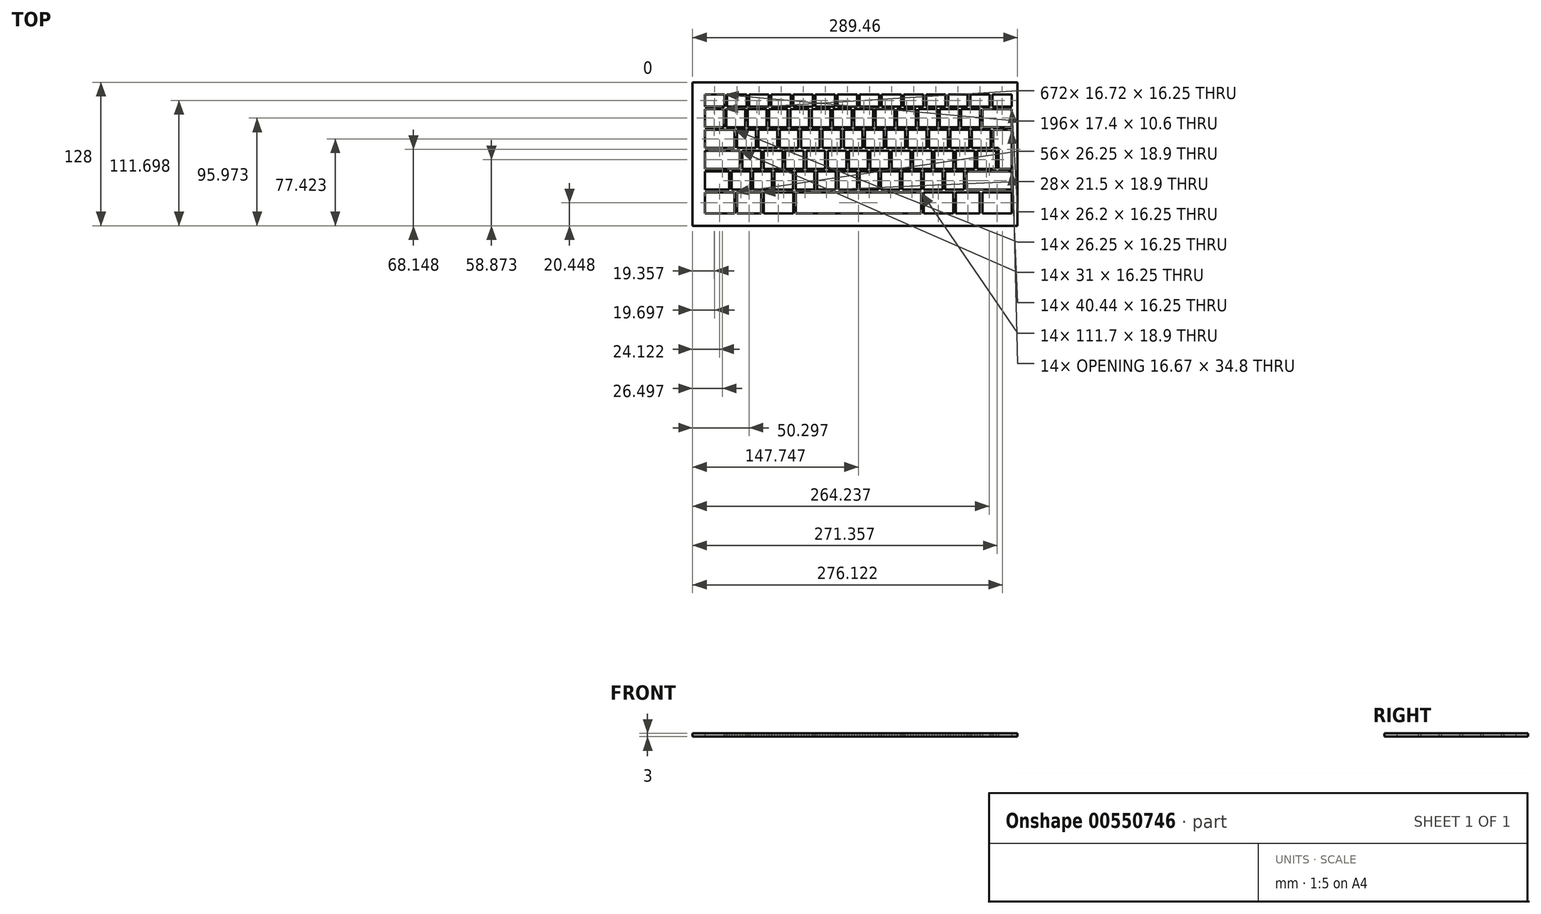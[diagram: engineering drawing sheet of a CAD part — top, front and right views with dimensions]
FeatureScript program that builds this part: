
annotation { "Feature Type Name" : "Feature", "Feature Type Description" : "" }
export const myFeature = defineFeature(function(context is Context, id is Id, definition is map)
    precondition{}
    {
        {
            var Q0;
            Q0=qCreatedBy(makeId("Top.planeOp"),FACE);
            var sketch = newSketch(context, id + "F0", { "sketchPlane" : qUnion([Q0])});
            skLineSegment(sketch, "E0.bottom", {"start": v(-207.41, -87.25) * mm, "end": v(222.59, -87.25) * mm, "construction": true});
            skLineSegment(sketch, "E0.top", {"start": v(-207.41, -201.25) * mm, "end": v(222.59, -201.25) * mm, "construction": true});
            skLineSegment(sketch, "E0.left", {"start": v(-207.41, -87.25) * mm, "end": v(-207.41, -201.25) * mm, "construction": true});
            skLineSegment(sketch, "E1.bottom", {"start": v(-203.41, -91.25) * mm, "end": v(-186.01, -91.25) * mm});
            skLineSegment(sketch, "E1.top", {"start": v(-203.41, -101.85) * mm, "end": v(-186.01, -101.85) * mm});
            skLineSegment(sketch, "E1.left", {"start": v(-203.41, -91.25) * mm, "end": v(-203.41, -101.85) * mm});
            skLineSegment(sketch, "E1.right", {"start": v(-186.01, -91.25) * mm, "end": v(-186.01, -101.85) * mm});
            skPoint(sketch, "E1.middle", {"position": v(-194.71, -96.55) * mm});
            skLineSegment(sketch, "E2.1.0.0", {"start": v(-166.31, -91.25) * mm, "end": v(-166.31, -101.85) * mm});
            skPoint(sketch, "E2.1.0.1", {"position": v(-175.01, -96.55) * mm});
            skLineSegment(sketch, "E2.1.0.2", {"start": v(-183.71, -91.25) * mm, "end": v(-183.71, -101.85) * mm});
            skLineSegment(sketch, "E2.1.0.3", {"start": v(-183.71, -101.85) * mm, "end": v(-166.31, -101.85) * mm});
            skLineSegment(sketch, "E2.1.0.4", {"start": v(-183.71, -91.25) * mm, "end": v(-166.31, -91.25) * mm});
            skLineSegment(sketch, "E2.2.0.0", {"start": v(-146.61, -91.25) * mm, "end": v(-146.61, -101.85) * mm});
            skPoint(sketch, "E2.2.0.1", {"position": v(-155.31, -96.55) * mm});
            skLineSegment(sketch, "E2.2.0.2", {"start": v(-164.01, -91.25) * mm, "end": v(-164.01, -101.85) * mm});
            skLineSegment(sketch, "E2.2.0.3", {"start": v(-164.01, -101.85) * mm, "end": v(-146.61, -101.85) * mm});
            skLineSegment(sketch, "E2.2.0.4", {"start": v(-164.01, -91.25) * mm, "end": v(-146.61, -91.25) * mm});
            skLineSegment(sketch, "E2.3.0.0", {"start": v(-126.91, -91.25) * mm, "end": v(-126.91, -101.85) * mm});
            skPoint(sketch, "E2.3.0.1", {"position": v(-135.61, -96.55) * mm});
            skLineSegment(sketch, "E2.3.0.2", {"start": v(-144.31, -91.25) * mm, "end": v(-144.31, -101.85) * mm});
            skLineSegment(sketch, "E2.3.0.3", {"start": v(-144.31, -101.85) * mm, "end": v(-126.91, -101.85) * mm});
            skLineSegment(sketch, "E2.3.0.4", {"start": v(-144.31, -91.25) * mm, "end": v(-126.91, -91.25) * mm});
            skLineSegment(sketch, "E2.4.0.0", {"start": v(-107.21, -91.25) * mm, "end": v(-107.21, -101.85) * mm});
            skPoint(sketch, "E2.4.0.1", {"position": v(-115.91, -96.55) * mm});
            skLineSegment(sketch, "E2.4.0.2", {"start": v(-124.61, -91.25) * mm, "end": v(-124.61, -101.85) * mm});
            skLineSegment(sketch, "E2.4.0.3", {"start": v(-124.61, -101.85) * mm, "end": v(-107.21, -101.85) * mm});
            skLineSegment(sketch, "E2.4.0.4", {"start": v(-124.61, -91.25) * mm, "end": v(-107.21, -91.25) * mm});
            skLineSegment(sketch, "E2.5.0.0", {"start": v(-87.51, -91.25) * mm, "end": v(-87.51, -101.85) * mm});
            skPoint(sketch, "E2.5.0.1", {"position": v(-96.21, -96.55) * mm});
            skLineSegment(sketch, "E2.5.0.2", {"start": v(-104.91, -91.25) * mm, "end": v(-104.91, -101.85) * mm});
            skLineSegment(sketch, "E2.5.0.3", {"start": v(-104.91, -101.85) * mm, "end": v(-87.51, -101.85) * mm});
            skLineSegment(sketch, "E2.5.0.4", {"start": v(-104.91, -91.25) * mm, "end": v(-87.51, -91.25) * mm});
            skLineSegment(sketch, "E2.6.0.0", {"start": v(-67.81, -91.25) * mm, "end": v(-67.81, -101.85) * mm});
            skPoint(sketch, "E2.6.0.1", {"position": v(-76.51, -96.55) * mm});
            skLineSegment(sketch, "E2.6.0.2", {"start": v(-85.21, -91.25) * mm, "end": v(-85.21, -101.85) * mm});
            skLineSegment(sketch, "E2.6.0.3", {"start": v(-85.21, -101.85) * mm, "end": v(-67.81, -101.85) * mm});
            skLineSegment(sketch, "E2.6.0.4", {"start": v(-85.21, -91.25) * mm, "end": v(-67.81, -91.25) * mm});
            skLineSegment(sketch, "E2.7.0.0", {"start": v(-48.11, -91.25) * mm, "end": v(-48.11, -101.85) * mm});
            skPoint(sketch, "E2.7.0.1", {"position": v(-56.81, -96.55) * mm});
            skLineSegment(sketch, "E2.7.0.2", {"start": v(-65.51, -91.25) * mm, "end": v(-65.51, -101.85) * mm});
            skLineSegment(sketch, "E2.7.0.3", {"start": v(-65.51, -101.85) * mm, "end": v(-48.11, -101.85) * mm});
            skLineSegment(sketch, "E2.7.0.4", {"start": v(-65.51, -91.25) * mm, "end": v(-48.11, -91.25) * mm});
            skLineSegment(sketch, "E2.8.0.0", {"start": v(-28.41, -91.25) * mm, "end": v(-28.41, -101.85) * mm});
            skPoint(sketch, "E2.8.0.1", {"position": v(-37.11, -96.55) * mm});
            skLineSegment(sketch, "E2.8.0.2", {"start": v(-45.81, -91.25) * mm, "end": v(-45.81, -101.85) * mm});
            skLineSegment(sketch, "E2.8.0.3", {"start": v(-45.81, -101.85) * mm, "end": v(-28.41, -101.85) * mm});
            skLineSegment(sketch, "E2.8.0.4", {"start": v(-45.81, -91.25) * mm, "end": v(-28.41, -91.25) * mm});
            skLineSegment(sketch, "E2.9.0.0", {"start": v(-8.71, -91.25) * mm, "end": v(-8.71, -101.85) * mm});
            skPoint(sketch, "E2.9.0.1", {"position": v(-17.41, -96.55) * mm});
            skLineSegment(sketch, "E2.9.0.2", {"start": v(-26.11, -91.25) * mm, "end": v(-26.11, -101.85) * mm});
            skLineSegment(sketch, "E2.9.0.3", {"start": v(-26.11, -101.85) * mm, "end": v(-8.71, -101.85) * mm});
            skLineSegment(sketch, "E2.9.0.4", {"start": v(-26.11, -91.25) * mm, "end": v(-8.71, -91.25) * mm});
            skLineSegment(sketch, "E2.10.0.0", {"start": v(10.99, -91.25) * mm, "end": v(10.99, -101.85) * mm});
            skPoint(sketch, "E2.10.0.1", {"position": v(2.29, -96.55) * mm});
            skLineSegment(sketch, "E2.10.0.2", {"start": v(-6.41, -91.25) * mm, "end": v(-6.41, -101.85) * mm});
            skLineSegment(sketch, "E2.10.0.3", {"start": v(-6.41, -101.85) * mm, "end": v(10.99, -101.85) * mm});
            skLineSegment(sketch, "E2.10.0.4", {"start": v(-6.41, -91.25) * mm, "end": v(10.99, -91.25) * mm});
            skLineSegment(sketch, "E2.11.0.0", {"start": v(30.69, -91.25) * mm, "end": v(30.69, -101.85) * mm});
            skPoint(sketch, "E2.11.0.1", {"position": v(21.99, -96.55) * mm});
            skLineSegment(sketch, "E2.11.0.2", {"start": v(13.29, -91.25) * mm, "end": v(13.29, -101.85) * mm});
            skLineSegment(sketch, "E2.11.0.3", {"start": v(13.29, -101.85) * mm, "end": v(30.69, -101.85) * mm});
            skLineSegment(sketch, "E2.11.0.4", {"start": v(13.29, -91.25) * mm, "end": v(30.69, -91.25) * mm});
            skLineSegment(sketch, "E2.12.0.0", {"start": v(50.39, -91.25) * mm, "end": v(50.39, -101.85) * mm});
            skPoint(sketch, "E2.12.0.1", {"position": v(41.69, -96.55) * mm});
            skLineSegment(sketch, "E2.12.0.2", {"start": v(32.99, -91.25) * mm, "end": v(32.99, -101.85) * mm});
            skLineSegment(sketch, "E2.12.0.3", {"start": v(32.99, -101.85) * mm, "end": v(50.39, -101.85) * mm});
            skLineSegment(sketch, "E2.12.0.4", {"start": v(32.99, -91.25) * mm, "end": v(50.39, -91.25) * mm});
            skLineSegment(sketch, "E2.13.0.0", {"start": v(70.09, -91.25) * mm, "end": v(70.09, -101.85) * mm});
            skPoint(sketch, "E2.13.0.1", {"position": v(61.39, -96.55) * mm});
            skLineSegment(sketch, "E2.13.0.2", {"start": v(52.69, -91.25) * mm, "end": v(52.69, -101.85) * mm});
            skLineSegment(sketch, "E2.13.0.3", {"start": v(52.69, -101.85) * mm, "end": v(70.09, -101.85) * mm});
            skLineSegment(sketch, "E2.13.0.4", {"start": v(52.69, -91.25) * mm, "end": v(70.09, -91.25) * mm});
            skLineSegment(sketch, "E3.bottom", {"start": v(-203.41, -104.15) * mm, "end": v(-186.7, -104.15) * mm});
            skLineSegment(sketch, "E3.top", {"start": v(-203.41, -120.4) * mm, "end": v(-186.7, -120.4) * mm});
            skLineSegment(sketch, "E3.left", {"start": v(-203.41, -104.15) * mm, "end": v(-203.41, -120.4) * mm});
            skLineSegment(sketch, "E3.right", {"start": v(-186.7, -104.15) * mm, "end": v(-186.7, -120.4) * mm});
            skPoint(sketch, "E3.middle", {"position": v(-195.05, -112.28) * mm});
            skPoint(sketch, "E4.1.0.0", {"position": v(-176.03, -112.28) * mm});
            skLineSegment(sketch, "E4.1.0.1", {"start": v(-167.67, -104.15) * mm, "end": v(-167.67, -120.4) * mm});
            skLineSegment(sketch, "E4.1.0.2", {"start": v(-184.4, -104.15) * mm, "end": v(-167.67, -104.15) * mm});
            skLineSegment(sketch, "E4.1.0.3", {"start": v(-184.4, -104.15) * mm, "end": v(-184.4, -120.4) * mm});
            skLineSegment(sketch, "E4.1.0.4", {"start": v(-184.4, -120.4) * mm, "end": v(-167.67, -120.4) * mm});
            skPoint(sketch, "E4.2.0.0", {"position": v(-157.01, -112.28) * mm});
            skLineSegment(sketch, "E4.2.0.1", {"start": v(-148.65, -104.15) * mm, "end": v(-148.65, -120.4) * mm});
            skLineSegment(sketch, "E4.2.0.2", {"start": v(-165.37, -104.15) * mm, "end": v(-148.65, -104.15) * mm});
            skLineSegment(sketch, "E4.2.0.3", {"start": v(-165.37, -104.15) * mm, "end": v(-165.37, -120.4) * mm});
            skLineSegment(sketch, "E4.2.0.4", {"start": v(-165.37, -120.4) * mm, "end": v(-148.65, -120.4) * mm});
            skPoint(sketch, "E4.3.0.0", {"position": v(-138, -112.28) * mm});
            skLineSegment(sketch, "E4.3.0.1", {"start": v(-129.63, -104.15) * mm, "end": v(-129.63, -120.4) * mm});
            skLineSegment(sketch, "E4.3.0.2", {"start": v(-146.35, -104.15) * mm, "end": v(-129.63, -104.15) * mm});
            skLineSegment(sketch, "E4.3.0.3", {"start": v(-146.35, -104.15) * mm, "end": v(-146.35, -120.4) * mm});
            skLineSegment(sketch, "E4.3.0.4", {"start": v(-146.35, -120.4) * mm, "end": v(-129.63, -120.4) * mm});
            skPoint(sketch, "E4.4.0.0", {"position": v(-118.97, -112.28) * mm});
            skLineSegment(sketch, "E4.4.0.1", {"start": v(-110.61, -104.15) * mm, "end": v(-110.61, -120.4) * mm});
            skLineSegment(sketch, "E4.4.0.2", {"start": v(-127.33, -104.15) * mm, "end": v(-110.61, -104.15) * mm});
            skLineSegment(sketch, "E4.4.0.3", {"start": v(-127.33, -104.15) * mm, "end": v(-127.33, -120.4) * mm});
            skLineSegment(sketch, "E4.4.0.4", {"start": v(-127.33, -120.4) * mm, "end": v(-110.61, -120.4) * mm});
            skPoint(sketch, "E4.5.0.0", {"position": v(-99.95, -112.28) * mm});
            skLineSegment(sketch, "E4.5.0.1", {"start": v(-91.6, -104.15) * mm, "end": v(-91.6, -120.4) * mm});
            skLineSegment(sketch, "E4.5.0.2", {"start": v(-108.31, -104.15) * mm, "end": v(-91.6, -104.15) * mm});
            skLineSegment(sketch, "E4.5.0.3", {"start": v(-108.31, -104.15) * mm, "end": v(-108.31, -120.4) * mm});
            skLineSegment(sketch, "E4.5.0.4", {"start": v(-108.31, -120.4) * mm, "end": v(-91.6, -120.4) * mm});
            skPoint(sketch, "E4.6.0.0", {"position": v(-80.93, -112.28) * mm});
            skLineSegment(sketch, "E4.6.0.1", {"start": v(-72.57, -104.15) * mm, "end": v(-72.57, -120.4) * mm});
            skLineSegment(sketch, "E4.6.0.2", {"start": v(-89.3, -104.15) * mm, "end": v(-72.57, -104.15) * mm});
            skLineSegment(sketch, "E4.6.0.3", {"start": v(-89.3, -104.15) * mm, "end": v(-89.3, -120.4) * mm});
            skLineSegment(sketch, "E4.6.0.4", {"start": v(-89.3, -120.4) * mm, "end": v(-72.57, -120.4) * mm});
            skPoint(sketch, "E4.7.0.0", {"position": v(-61.91, -112.28) * mm});
            skLineSegment(sketch, "E4.7.0.1", {"start": v(-53.55, -104.15) * mm, "end": v(-53.55, -120.4) * mm});
            skLineSegment(sketch, "E4.7.0.2", {"start": v(-70.27, -104.15) * mm, "end": v(-53.55, -104.15) * mm});
            skLineSegment(sketch, "E4.7.0.3", {"start": v(-70.27, -104.15) * mm, "end": v(-70.27, -120.4) * mm});
            skLineSegment(sketch, "E4.7.0.4", {"start": v(-70.27, -120.4) * mm, "end": v(-53.55, -120.4) * mm});
            skPoint(sketch, "E4.8.0.0", {"position": v(-42.9, -112.28) * mm});
            skLineSegment(sketch, "E4.8.0.1", {"start": v(-34.53, -104.15) * mm, "end": v(-34.53, -120.4) * mm});
            skLineSegment(sketch, "E4.8.0.2", {"start": v(-51.25, -104.15) * mm, "end": v(-34.53, -104.15) * mm});
            skLineSegment(sketch, "E4.8.0.3", {"start": v(-51.25, -104.15) * mm, "end": v(-51.25, -120.4) * mm});
            skLineSegment(sketch, "E4.8.0.4", {"start": v(-51.25, -120.4) * mm, "end": v(-34.53, -120.4) * mm});
            skPoint(sketch, "E4.9.0.0", {"position": v(-23.87, -112.28) * mm});
            skLineSegment(sketch, "E4.9.0.1", {"start": v(-15.51, -104.15) * mm, "end": v(-15.51, -120.4) * mm});
            skLineSegment(sketch, "E4.9.0.2", {"start": v(-32.23, -104.15) * mm, "end": v(-15.51, -104.15) * mm});
            skLineSegment(sketch, "E4.9.0.3", {"start": v(-32.23, -104.15) * mm, "end": v(-32.23, -120.4) * mm});
            skLineSegment(sketch, "E4.9.0.4", {"start": v(-32.23, -120.4) * mm, "end": v(-15.51, -120.4) * mm});
            skPoint(sketch, "E4.10.0.0", {"position": v(-4.85, -112.28) * mm});
            skLineSegment(sketch, "E4.10.0.1", {"start": v(3.5, -104.15) * mm, "end": v(3.5, -120.4) * mm});
            skLineSegment(sketch, "E4.10.0.2", {"start": v(-13.21, -104.15) * mm, "end": v(3.5, -104.15) * mm});
            skLineSegment(sketch, "E4.10.0.3", {"start": v(-13.21, -104.15) * mm, "end": v(-13.21, -120.4) * mm});
            skLineSegment(sketch, "E4.10.0.4", {"start": v(-13.21, -120.4) * mm, "end": v(3.5, -120.4) * mm});
            skPoint(sketch, "E4.11.0.0", {"position": v(14.17, -112.28) * mm});
            skLineSegment(sketch, "E4.11.0.1", {"start": v(22.53, -104.15) * mm, "end": v(22.53, -120.4) * mm});
            skLineSegment(sketch, "E4.11.0.2", {"start": v(5.8, -104.15) * mm, "end": v(22.53, -104.15) * mm});
            skLineSegment(sketch, "E4.11.0.3", {"start": v(5.8, -104.15) * mm, "end": v(5.8, -120.4) * mm});
            skLineSegment(sketch, "E4.11.0.4", {"start": v(5.8, -120.4) * mm, "end": v(22.53, -120.4) * mm});
            skPoint(sketch, "E4.12.0.0", {"position": v(33.19, -112.28) * mm});
            skLineSegment(sketch, "E4.12.0.1", {"start": v(41.55, -104.15) * mm, "end": v(41.55, -120.4) * mm});
            skLineSegment(sketch, "E4.12.0.2", {"start": v(24.83, -104.15) * mm, "end": v(41.55, -104.15) * mm});
            skLineSegment(sketch, "E4.12.0.3", {"start": v(24.83, -104.15) * mm, "end": v(24.83, -120.4) * mm});
            skLineSegment(sketch, "E4.12.0.4", {"start": v(24.83, -120.4) * mm, "end": v(41.55, -120.4) * mm});
            skLineSegment(sketch, "E5.bottom", {"start": v(43.85, -104.15) * mm, "end": v(70.05, -104.15) * mm});
            skLineSegment(sketch, "E5.top", {"start": v(43.85, -120.4) * mm, "end": v(70.05, -120.4) * mm});
            skLineSegment(sketch, "E5.left", {"start": v(43.85, -104.15) * mm, "end": v(43.85, -120.4) * mm});
            skLineSegment(sketch, "E5.right", {"start": v(70.05, -104.15) * mm, "end": v(70.05, -120.4) * mm});
            skPoint(sketch, "E5.middle", {"position": v(56.95, -112.28) * mm});
            skLineSegment(sketch, "E6.bottom", {"start": v(-203.41, -122.7) * mm, "end": v(-177.16, -122.7) * mm});
            skLineSegment(sketch, "E6.top", {"start": v(-203.41, -138.95) * mm, "end": v(-177.16, -138.95) * mm});
            skLineSegment(sketch, "E6.left", {"start": v(-203.41, -122.7) * mm, "end": v(-203.41, -138.95) * mm});
            skLineSegment(sketch, "E6.right", {"start": v(-177.16, -122.7) * mm, "end": v(-177.16, -138.95) * mm});
            skPoint(sketch, "E6.middle", {"position": v(-190.29, -130.83) * mm});
            skLineSegment(sketch, "E7.bottom", {"start": v(-174.86, -122.7) * mm, "end": v(-158.14, -122.7) * mm});
            skLineSegment(sketch, "E7.top", {"start": v(-174.86, -138.95) * mm, "end": v(-158.14, -138.95) * mm});
            skLineSegment(sketch, "E7.left", {"start": v(-174.86, -122.7) * mm, "end": v(-174.86, -138.95) * mm});
            skLineSegment(sketch, "E7.right", {"start": v(-158.14, -122.7) * mm, "end": v(-158.14, -138.95) * mm});
            skPoint(sketch, "E7.middle", {"position": v(-166.5, -130.83) * mm});
            skLineSegment(sketch, "E8.1.0.0", {"start": v(-139.12, -122.7) * mm, "end": v(-139.12, -138.95) * mm});
            skLineSegment(sketch, "E8.1.0.1", {"start": v(-155.84, -122.7) * mm, "end": v(-155.84, -138.95) * mm});
            skLineSegment(sketch, "E8.1.0.2", {"start": v(-155.84, -122.7) * mm, "end": v(-139.12, -122.7) * mm});
            skPoint(sketch, "E8.1.0.3", {"position": v(-147.48, -130.83) * mm});
            skLineSegment(sketch, "E8.1.0.4", {"start": v(-155.84, -138.95) * mm, "end": v(-139.12, -138.95) * mm});
            skLineSegment(sketch, "E8.2.0.0", {"start": v(-120.1, -122.7) * mm, "end": v(-120.1, -138.95) * mm});
            skLineSegment(sketch, "E8.2.0.1", {"start": v(-136.82, -122.7) * mm, "end": v(-136.82, -138.95) * mm});
            skLineSegment(sketch, "E8.2.0.2", {"start": v(-136.82, -122.7) * mm, "end": v(-120.1, -122.7) * mm});
            skPoint(sketch, "E8.2.0.3", {"position": v(-128.46, -130.83) * mm});
            skLineSegment(sketch, "E8.2.0.4", {"start": v(-136.82, -138.95) * mm, "end": v(-120.1, -138.95) * mm});
            skLineSegment(sketch, "E8.3.0.0", {"start": v(-101.08, -122.7) * mm, "end": v(-101.08, -138.95) * mm});
            skLineSegment(sketch, "E8.3.0.1", {"start": v(-117.8, -122.7) * mm, "end": v(-117.8, -138.95) * mm});
            skLineSegment(sketch, "E8.3.0.2", {"start": v(-117.8, -122.7) * mm, "end": v(-101.08, -122.7) * mm});
            skPoint(sketch, "E8.3.0.3", {"position": v(-109.44, -130.83) * mm});
            skLineSegment(sketch, "E8.3.0.4", {"start": v(-117.8, -138.95) * mm, "end": v(-101.08, -138.95) * mm});
            skLineSegment(sketch, "E8.4.0.0", {"start": v(-82.06, -122.7) * mm, "end": v(-82.06, -138.95) * mm});
            skLineSegment(sketch, "E8.4.0.1", {"start": v(-98.78, -122.7) * mm, "end": v(-98.78, -138.95) * mm});
            skLineSegment(sketch, "E8.4.0.2", {"start": v(-98.78, -122.7) * mm, "end": v(-82.06, -122.7) * mm});
            skPoint(sketch, "E8.4.0.3", {"position": v(-90.42, -130.83) * mm});
            skLineSegment(sketch, "E8.4.0.4", {"start": v(-98.78, -138.95) * mm, "end": v(-82.06, -138.95) * mm});
            skLineSegment(sketch, "E8.5.0.0", {"start": v(-63.04, -122.7) * mm, "end": v(-63.04, -138.95) * mm});
            skLineSegment(sketch, "E8.5.0.1", {"start": v(-79.76, -122.7) * mm, "end": v(-79.76, -138.95) * mm});
            skLineSegment(sketch, "E8.5.0.2", {"start": v(-79.76, -122.7) * mm, "end": v(-63.04, -122.7) * mm});
            skPoint(sketch, "E8.5.0.3", {"position": v(-71.4, -130.83) * mm});
            skLineSegment(sketch, "E8.5.0.4", {"start": v(-79.76, -138.95) * mm, "end": v(-63.04, -138.95) * mm});
            skLineSegment(sketch, "E8.6.0.0", {"start": v(-44.02, -122.7) * mm, "end": v(-44.02, -138.95) * mm});
            skLineSegment(sketch, "E8.6.0.1", {"start": v(-60.74, -122.7) * mm, "end": v(-60.74, -138.95) * mm});
            skLineSegment(sketch, "E8.6.0.2", {"start": v(-60.74, -122.7) * mm, "end": v(-44.02, -122.7) * mm});
            skPoint(sketch, "E8.6.0.3", {"position": v(-52.38, -130.83) * mm});
            skLineSegment(sketch, "E8.6.0.4", {"start": v(-60.74, -138.95) * mm, "end": v(-44.02, -138.95) * mm});
            skLineSegment(sketch, "E8.7.0.0", {"start": v(-25, -122.7) * mm, "end": v(-25, -138.95) * mm});
            skLineSegment(sketch, "E8.7.0.1", {"start": v(-41.72, -122.7) * mm, "end": v(-41.72, -138.95) * mm});
            skLineSegment(sketch, "E8.7.0.2", {"start": v(-41.72, -122.7) * mm, "end": v(-25, -122.7) * mm});
            skPoint(sketch, "E8.7.0.3", {"position": v(-33.36, -130.83) * mm});
            skLineSegment(sketch, "E8.7.0.4", {"start": v(-41.72, -138.95) * mm, "end": v(-25, -138.95) * mm});
            skLineSegment(sketch, "E8.8.0.0", {"start": v(-5.98, -122.7) * mm, "end": v(-5.98, -138.95) * mm});
            skLineSegment(sketch, "E8.8.0.1", {"start": v(-22.7, -122.7) * mm, "end": v(-22.7, -138.95) * mm});
            skLineSegment(sketch, "E8.8.0.2", {"start": v(-22.7, -122.7) * mm, "end": v(-5.98, -122.7) * mm});
            skPoint(sketch, "E8.8.0.3", {"position": v(-14.34, -130.83) * mm});
            skLineSegment(sketch, "E8.8.0.4", {"start": v(-22.7, -138.95) * mm, "end": v(-5.98, -138.95) * mm});
            skLineSegment(sketch, "E8.9.0.0", {"start": v(13.04, -122.7) * mm, "end": v(13.04, -138.95) * mm});
            skLineSegment(sketch, "E8.9.0.1", {"start": v(-3.68, -122.7) * mm, "end": v(-3.68, -138.95) * mm});
            skLineSegment(sketch, "E8.9.0.2", {"start": v(-3.68, -122.7) * mm, "end": v(13.04, -122.7) * mm});
            skPoint(sketch, "E8.9.0.3", {"position": v(4.68, -130.83) * mm});
            skLineSegment(sketch, "E8.9.0.4", {"start": v(-3.68, -138.95) * mm, "end": v(13.04, -138.95) * mm});
            skLineSegment(sketch, "E8.10.0.0", {"start": v(32.06, -122.7) * mm, "end": v(32.06, -138.95) * mm});
            skLineSegment(sketch, "E8.10.0.1", {"start": v(15.34, -122.7) * mm, "end": v(15.34, -138.95) * mm});
            skLineSegment(sketch, "E8.10.0.2", {"start": v(15.34, -122.7) * mm, "end": v(32.06, -122.7) * mm});
            skPoint(sketch, "E8.10.0.3", {"position": v(23.7, -130.83) * mm});
            skLineSegment(sketch, "E8.10.0.4", {"start": v(15.34, -138.95) * mm, "end": v(32.06, -138.95) * mm});
            skLineSegment(sketch, "E8.11.0.0", {"start": v(51.08, -122.7) * mm, "end": v(51.08, -138.95) * mm});
            skLineSegment(sketch, "E8.11.0.1", {"start": v(34.36, -122.7) * mm, "end": v(34.36, -138.95) * mm});
            skLineSegment(sketch, "E8.11.0.2", {"start": v(34.36, -122.7) * mm, "end": v(51.08, -122.7) * mm});
            skPoint(sketch, "E8.11.0.3", {"position": v(42.72, -130.83) * mm});
            skLineSegment(sketch, "E8.11.0.4", {"start": v(34.36, -138.95) * mm, "end": v(51.08, -138.95) * mm});
            skLineSegment(sketch, "E9.bottom", {"start": v(-203.41, -141.25) * mm, "end": v(-172.41, -141.25) * mm});
            skLineSegment(sketch, "E9.top", {"start": v(-203.41, -157.5) * mm, "end": v(-172.41, -157.5) * mm});
            skLineSegment(sketch, "E9.left", {"start": v(-203.41, -141.25) * mm, "end": v(-203.41, -157.5) * mm});
            skLineSegment(sketch, "E9.right", {"start": v(-172.41, -141.25) * mm, "end": v(-172.41, -157.5) * mm});
            skPoint(sketch, "E9.middle", {"position": v(-187.91, -149.38) * mm});
            skLineSegment(sketch, "E10.bottom", {"start": v(-170.11, -141.25) * mm, "end": v(-153.4, -141.25) * mm});
            skLineSegment(sketch, "E10.top", {"start": v(-170.11, -157.5) * mm, "end": v(-153.4, -157.5) * mm});
            skLineSegment(sketch, "E10.left", {"start": v(-170.11, -141.25) * mm, "end": v(-170.11, -157.5) * mm});
            skLineSegment(sketch, "E10.right", {"start": v(-153.4, -141.25) * mm, "end": v(-153.4, -157.5) * mm});
            skPoint(sketch, "E10.middle", {"position": v(-161.75, -149.38) * mm});
            skLineSegment(sketch, "E11.1.0.0", {"start": v(-151.1, -157.5) * mm, "end": v(-134.37, -157.5) * mm});
            skPoint(sketch, "E11.1.0.1", {"position": v(-142.73, -149.38) * mm});
            skLineSegment(sketch, "E11.1.0.2", {"start": v(-151.1, -141.25) * mm, "end": v(-134.37, -141.25) * mm});
            skLineSegment(sketch, "E11.1.0.3", {"start": v(-134.37, -141.25) * mm, "end": v(-134.37, -157.5) * mm});
            skLineSegment(sketch, "E11.1.0.4", {"start": v(-151.1, -141.25) * mm, "end": v(-151.1, -157.5) * mm});
            skLineSegment(sketch, "E11.2.0.0", {"start": v(-132.07, -157.5) * mm, "end": v(-115.35, -157.5) * mm});
            skPoint(sketch, "E11.2.0.1", {"position": v(-123.71, -149.38) * mm});
            skLineSegment(sketch, "E11.2.0.2", {"start": v(-132.07, -141.25) * mm, "end": v(-115.35, -141.25) * mm});
            skLineSegment(sketch, "E11.2.0.3", {"start": v(-115.35, -141.25) * mm, "end": v(-115.35, -157.5) * mm});
            skLineSegment(sketch, "E11.2.0.4", {"start": v(-132.07, -141.25) * mm, "end": v(-132.07, -157.5) * mm});
            skLineSegment(sketch, "E11.3.0.0", {"start": v(-113.05, -157.5) * mm, "end": v(-96.33, -157.5) * mm});
            skPoint(sketch, "E11.3.0.1", {"position": v(-104.7, -149.38) * mm});
            skLineSegment(sketch, "E11.3.0.2", {"start": v(-113.05, -141.25) * mm, "end": v(-96.33, -141.25) * mm});
            skLineSegment(sketch, "E11.3.0.3", {"start": v(-96.33, -141.25) * mm, "end": v(-96.33, -157.5) * mm});
            skLineSegment(sketch, "E11.3.0.4", {"start": v(-113.05, -141.25) * mm, "end": v(-113.05, -157.5) * mm});
            skLineSegment(sketch, "E11.4.0.0", {"start": v(-94.03, -157.5) * mm, "end": v(-77.31, -157.5) * mm});
            skPoint(sketch, "E11.4.0.1", {"position": v(-85.67, -149.38) * mm});
            skLineSegment(sketch, "E11.4.0.2", {"start": v(-94.03, -141.25) * mm, "end": v(-77.31, -141.25) * mm});
            skLineSegment(sketch, "E11.4.0.3", {"start": v(-77.31, -141.25) * mm, "end": v(-77.31, -157.5) * mm});
            skLineSegment(sketch, "E11.4.0.4", {"start": v(-94.03, -141.25) * mm, "end": v(-94.03, -157.5) * mm});
            skLineSegment(sketch, "E11.5.0.0", {"start": v(-75.01, -157.5) * mm, "end": v(-58.3, -157.5) * mm});
            skPoint(sketch, "E11.5.0.1", {"position": v(-66.65, -149.38) * mm});
            skLineSegment(sketch, "E11.5.0.2", {"start": v(-75.01, -141.25) * mm, "end": v(-58.3, -141.25) * mm});
            skLineSegment(sketch, "E11.5.0.3", {"start": v(-58.3, -141.25) * mm, "end": v(-58.3, -157.5) * mm});
            skLineSegment(sketch, "E11.5.0.4", {"start": v(-75.01, -141.25) * mm, "end": v(-75.01, -157.5) * mm});
            skLineSegment(sketch, "E11.6.0.0", {"start": v(-56, -157.5) * mm, "end": v(-39.27, -157.5) * mm});
            skPoint(sketch, "E11.6.0.1", {"position": v(-47.63, -149.38) * mm});
            skLineSegment(sketch, "E11.6.0.2", {"start": v(-56, -141.25) * mm, "end": v(-39.27, -141.25) * mm});
            skLineSegment(sketch, "E11.6.0.3", {"start": v(-39.27, -141.25) * mm, "end": v(-39.27, -157.5) * mm});
            skLineSegment(sketch, "E11.6.0.4", {"start": v(-56, -141.25) * mm, "end": v(-56, -157.5) * mm});
            skLineSegment(sketch, "E11.7.0.0", {"start": v(-36.97, -157.5) * mm, "end": v(-20.25, -157.5) * mm});
            skPoint(sketch, "E11.7.0.1", {"position": v(-28.61, -149.38) * mm});
            skLineSegment(sketch, "E11.7.0.2", {"start": v(-36.97, -141.25) * mm, "end": v(-20.25, -141.25) * mm});
            skLineSegment(sketch, "E11.7.0.3", {"start": v(-20.25, -141.25) * mm, "end": v(-20.25, -157.5) * mm});
            skLineSegment(sketch, "E11.7.0.4", {"start": v(-36.97, -141.25) * mm, "end": v(-36.97, -157.5) * mm});
            skLineSegment(sketch, "E11.8.0.0", {"start": v(-17.95, -157.5) * mm, "end": v(-1.23, -157.5) * mm});
            skPoint(sketch, "E11.8.0.1", {"position": v(-9.6, -149.38) * mm});
            skLineSegment(sketch, "E11.8.0.2", {"start": v(-17.95, -141.25) * mm, "end": v(-1.23, -141.25) * mm});
            skLineSegment(sketch, "E11.8.0.3", {"start": v(-1.23, -141.25) * mm, "end": v(-1.23, -157.5) * mm});
            skLineSegment(sketch, "E11.8.0.4", {"start": v(-17.95, -141.25) * mm, "end": v(-17.95, -157.5) * mm});
            skLineSegment(sketch, "E11.9.0.0", {"start": v(1.07, -157.5) * mm, "end": v(17.79, -157.5) * mm});
            skPoint(sketch, "E11.9.0.1", {"position": v(9.43, -149.38) * mm});
            skLineSegment(sketch, "E11.9.0.2", {"start": v(1.07, -141.25) * mm, "end": v(17.79, -141.25) * mm});
            skLineSegment(sketch, "E11.9.0.3", {"start": v(17.79, -141.25) * mm, "end": v(17.79, -157.5) * mm});
            skLineSegment(sketch, "E11.9.0.4", {"start": v(1.07, -141.25) * mm, "end": v(1.07, -157.5) * mm});
            skLineSegment(sketch, "E11.10.0.0", {"start": v(20.09, -157.5) * mm, "end": v(36.8, -157.5) * mm});
            skPoint(sketch, "E11.10.0.1", {"position": v(28.45, -149.38) * mm});
            skLineSegment(sketch, "E11.10.0.2", {"start": v(20.09, -141.25) * mm, "end": v(36.8, -141.25) * mm});
            skLineSegment(sketch, "E11.10.0.3", {"start": v(36.8, -141.25) * mm, "end": v(36.8, -157.5) * mm});
            skLineSegment(sketch, "E11.10.0.4", {"start": v(20.09, -141.25) * mm, "end": v(20.09, -157.5) * mm});
            skLineSegment(sketch, "E11.11.0.0", {"start": v(39.1, -157.5) * mm, "end": v(55.83, -157.5) * mm});
            skPoint(sketch, "E11.11.0.1", {"position": v(47.47, -149.38) * mm});
            skLineSegment(sketch, "E11.11.0.2", {"start": v(39.1, -141.25) * mm, "end": v(55.83, -141.25) * mm});
            skLineSegment(sketch, "E11.11.0.3", {"start": v(55.83, -141.25) * mm, "end": v(55.83, -157.5) * mm});
            skLineSegment(sketch, "E11.11.0.4", {"start": v(39.1, -141.25) * mm, "end": v(39.1, -157.5) * mm});
            skLineSegment(sketch, "E12.bottom", {"start": v(-203.41, -159.8) * mm, "end": v(-181.91, -159.8) * mm});
            skLineSegment(sketch, "E12.top", {"start": v(-203.41, -176.05) * mm, "end": v(-181.91, -176.05) * mm});
            skLineSegment(sketch, "E12.left", {"start": v(-203.41, -159.8) * mm, "end": v(-203.41, -176.05) * mm});
            skLineSegment(sketch, "E12.right", {"start": v(-181.91, -159.8) * mm, "end": v(-181.91, -176.05) * mm});
            skPoint(sketch, "E12.middle", {"position": v(-192.66, -167.93) * mm});
            skLineSegment(sketch, "E13.bottom", {"start": v(-179.61, -159.8) * mm, "end": v(-162.9, -159.8) * mm});
            skLineSegment(sketch, "E13.top", {"start": v(-179.61, -176.05) * mm, "end": v(-162.9, -176.05) * mm});
            skLineSegment(sketch, "E13.left", {"start": v(-179.61, -159.8) * mm, "end": v(-179.61, -176.05) * mm});
            skLineSegment(sketch, "E13.right", {"start": v(-162.9, -159.8) * mm, "end": v(-162.9, -176.05) * mm});
            skPoint(sketch, "E13.middle", {"position": v(-171.25, -167.93) * mm});
            skLineSegment(sketch, "E14.1.0.0", {"start": v(-160.6, -159.8) * mm, "end": v(-160.6, -176.05) * mm});
            skLineSegment(sketch, "E14.1.0.1", {"start": v(-143.87, -159.8) * mm, "end": v(-143.87, -176.05) * mm});
            skLineSegment(sketch, "E14.1.0.2", {"start": v(-160.6, -176.05) * mm, "end": v(-143.87, -176.05) * mm});
            skPoint(sketch, "E14.1.0.3", {"position": v(-152.23, -167.93) * mm});
            skLineSegment(sketch, "E14.1.0.4", {"start": v(-160.6, -159.8) * mm, "end": v(-143.87, -159.8) * mm});
            skLineSegment(sketch, "E14.2.0.0", {"start": v(-141.57, -159.8) * mm, "end": v(-141.57, -176.05) * mm});
            skLineSegment(sketch, "E14.2.0.1", {"start": v(-124.85, -159.8) * mm, "end": v(-124.85, -176.05) * mm});
            skLineSegment(sketch, "E14.2.0.2", {"start": v(-141.57, -176.05) * mm, "end": v(-124.85, -176.05) * mm});
            skPoint(sketch, "E14.2.0.3", {"position": v(-133.21, -167.93) * mm});
            skLineSegment(sketch, "E14.2.0.4", {"start": v(-141.57, -159.8) * mm, "end": v(-124.85, -159.8) * mm});
            skLineSegment(sketch, "E14.3.0.0", {"start": v(-122.55, -159.8) * mm, "end": v(-122.55, -176.05) * mm});
            skLineSegment(sketch, "E14.3.0.1", {"start": v(-105.83, -159.8) * mm, "end": v(-105.83, -176.05) * mm});
            skLineSegment(sketch, "E14.3.0.2", {"start": v(-122.55, -176.05) * mm, "end": v(-105.83, -176.05) * mm});
            skPoint(sketch, "E14.3.0.3", {"position": v(-114.2, -167.93) * mm});
            skLineSegment(sketch, "E14.3.0.4", {"start": v(-122.55, -159.8) * mm, "end": v(-105.83, -159.8) * mm});
            skLineSegment(sketch, "E14.4.0.0", {"start": v(-103.53, -159.8) * mm, "end": v(-103.53, -176.05) * mm});
            skLineSegment(sketch, "E14.4.0.1", {"start": v(-86.81, -159.8) * mm, "end": v(-86.81, -176.05) * mm});
            skLineSegment(sketch, "E14.4.0.2", {"start": v(-103.53, -176.05) * mm, "end": v(-86.81, -176.05) * mm});
            skPoint(sketch, "E14.4.0.3", {"position": v(-95.17, -167.93) * mm});
            skLineSegment(sketch, "E14.4.0.4", {"start": v(-103.53, -159.8) * mm, "end": v(-86.81, -159.8) * mm});
            skLineSegment(sketch, "E14.5.0.0", {"start": v(-84.51, -159.8) * mm, "end": v(-84.51, -176.05) * mm});
            skLineSegment(sketch, "E14.5.0.1", {"start": v(-67.8, -159.8) * mm, "end": v(-67.8, -176.05) * mm});
            skLineSegment(sketch, "E14.5.0.2", {"start": v(-84.51, -176.05) * mm, "end": v(-67.8, -176.05) * mm});
            skPoint(sketch, "E14.5.0.3", {"position": v(-76.15, -167.93) * mm});
            skLineSegment(sketch, "E14.5.0.4", {"start": v(-84.51, -159.8) * mm, "end": v(-67.8, -159.8) * mm});
            skLineSegment(sketch, "E14.6.0.0", {"start": v(-65.5, -159.8) * mm, "end": v(-65.5, -176.05) * mm});
            skLineSegment(sketch, "E14.6.0.1", {"start": v(-48.77, -159.8) * mm, "end": v(-48.77, -176.05) * mm});
            skLineSegment(sketch, "E14.6.0.2", {"start": v(-65.5, -176.05) * mm, "end": v(-48.77, -176.05) * mm});
            skPoint(sketch, "E14.6.0.3", {"position": v(-57.13, -167.93) * mm});
            skLineSegment(sketch, "E14.6.0.4", {"start": v(-65.5, -159.8) * mm, "end": v(-48.77, -159.8) * mm});
            skLineSegment(sketch, "E14.7.0.0", {"start": v(-46.47, -159.8) * mm, "end": v(-46.47, -176.05) * mm});
            skLineSegment(sketch, "E14.7.0.1", {"start": v(-29.75, -159.8) * mm, "end": v(-29.75, -176.05) * mm});
            skLineSegment(sketch, "E14.7.0.2", {"start": v(-46.47, -176.05) * mm, "end": v(-29.75, -176.05) * mm});
            skPoint(sketch, "E14.7.0.3", {"position": v(-38.11, -167.93) * mm});
            skLineSegment(sketch, "E14.7.0.4", {"start": v(-46.47, -159.8) * mm, "end": v(-29.75, -159.8) * mm});
            skLineSegment(sketch, "E14.8.0.0", {"start": v(-27.45, -159.8) * mm, "end": v(-27.45, -176.05) * mm});
            skLineSegment(sketch, "E14.8.0.1", {"start": v(-10.73, -159.8) * mm, "end": v(-10.73, -176.05) * mm});
            skLineSegment(sketch, "E14.8.0.2", {"start": v(-27.45, -176.05) * mm, "end": v(-10.73, -176.05) * mm});
            skPoint(sketch, "E14.8.0.3", {"position": v(-19.1, -167.93) * mm});
            skLineSegment(sketch, "E14.8.0.4", {"start": v(-27.45, -159.8) * mm, "end": v(-10.73, -159.8) * mm});
            skLineSegment(sketch, "E14.9.0.0", {"start": v(-8.43, -159.8) * mm, "end": v(-8.43, -176.05) * mm});
            skLineSegment(sketch, "E14.9.0.1", {"start": v(8.29, -159.8) * mm, "end": v(8.29, -176.05) * mm});
            skLineSegment(sketch, "E14.9.0.2", {"start": v(-8.43, -176.05) * mm, "end": v(8.29, -176.05) * mm});
            skPoint(sketch, "E14.9.0.3", {"position": v(-0.07, -167.93) * mm});
            skLineSegment(sketch, "E14.9.0.4", {"start": v(-8.43, -159.8) * mm, "end": v(8.29, -159.8) * mm});
            skLineSegment(sketch, "E14.10.0.0", {"start": v(10.59, -159.8) * mm, "end": v(10.59, -176.05) * mm});
            skLineSegment(sketch, "E14.10.0.1", {"start": v(27.3, -159.8) * mm, "end": v(27.3, -176.05) * mm});
            skLineSegment(sketch, "E14.10.0.2", {"start": v(10.59, -176.05) * mm, "end": v(27.3, -176.05) * mm});
            skPoint(sketch, "E14.10.0.3", {"position": v(18.95, -167.93) * mm});
            skLineSegment(sketch, "E14.10.0.4", {"start": v(10.59, -159.8) * mm, "end": v(27.3, -159.8) * mm});
            skLineSegment(sketch, "E15.bottom", {"start": v(29.6, -159.8) * mm, "end": v(70.05, -159.8) * mm});
            skLineSegment(sketch, "E15.top", {"start": v(29.6, -176.05) * mm, "end": v(70.05, -176.05) * mm});
            skLineSegment(sketch, "E15.left", {"start": v(29.6, -159.8) * mm, "end": v(29.6, -176.05) * mm});
            skLineSegment(sketch, "E15.right", {"start": v(70.05, -159.8) * mm, "end": v(70.05, -176.05) * mm});
            skPoint(sketch, "E15.middle", {"position": v(49.83, -167.93) * mm});
            skLineSegment(sketch, "E16", {"start": v(70.05, -122.7) * mm, "end": v(70.05, -157.5) * mm});
            skLineSegment(sketch, "E17", {"start": v(70.05, -157.5) * mm, "end": v(58.13, -157.5) * mm});
            skLineSegment(sketch, "E18", {"start": v(58.13, -157.5) * mm, "end": v(58.13, -138.95) * mm});
            skLineSegment(sketch, "E19", {"start": v(58.13, -138.95) * mm, "end": v(53.38, -138.95) * mm});
            skLineSegment(sketch, "E20", {"start": v(53.38, -138.95) * mm, "end": v(53.38, -122.7) * mm});
            skLineSegment(sketch, "E21", {"start": v(53.38, -122.7) * mm, "end": v(70.05, -122.7) * mm});
            skLineSegment(sketch, "E22.bottom", {"start": v(-203.41, -178.35) * mm, "end": v(-177.16, -178.35) * mm});
            skLineSegment(sketch, "E22.top", {"start": v(-203.41, -197.25) * mm, "end": v(-177.16, -197.25) * mm});
            skLineSegment(sketch, "E22.left", {"start": v(-203.41, -178.35) * mm, "end": v(-203.41, -197.25) * mm});
            skLineSegment(sketch, "E22.right", {"start": v(-177.16, -178.35) * mm, "end": v(-177.16, -197.25) * mm});
            skPoint(sketch, "E22.middle", {"position": v(-190.29, -187.8) * mm});
            skLineSegment(sketch, "E23.bottom", {"start": v(-174.86, -178.35) * mm, "end": v(-153.36, -178.35) * mm});
            skLineSegment(sketch, "E23.top", {"start": v(-174.86, -197.25) * mm, "end": v(-153.36, -197.25) * mm});
            skLineSegment(sketch, "E23.left", {"start": v(-174.86, -178.35) * mm, "end": v(-174.86, -197.25) * mm});
            skLineSegment(sketch, "E23.right", {"start": v(-153.36, -178.35) * mm, "end": v(-153.36, -197.25) * mm});
            skPoint(sketch, "E23.middle", {"position": v(-164.11, -187.8) * mm});
            skLineSegment(sketch, "E24.bottom", {"start": v(-151.06, -178.35) * mm, "end": v(-124.81, -178.35) * mm});
            skLineSegment(sketch, "E24.top", {"start": v(-151.06, -197.25) * mm, "end": v(-124.81, -197.25) * mm});
            skLineSegment(sketch, "E24.left", {"start": v(-151.06, -178.35) * mm, "end": v(-151.06, -197.25) * mm});
            skLineSegment(sketch, "E24.right", {"start": v(-124.81, -178.35) * mm, "end": v(-124.81, -197.25) * mm});
            skPoint(sketch, "E24.middle", {"position": v(-137.94, -187.8) * mm});
            skLineSegment(sketch, "E25.bottom", {"start": v(-122.51, -178.35) * mm, "end": v(-10.81, -178.35) * mm});
            skLineSegment(sketch, "E25.top", {"start": v(-122.51, -197.25) * mm, "end": v(-10.81, -197.25) * mm});
            skLineSegment(sketch, "E25.left", {"start": v(-122.51, -178.35) * mm, "end": v(-122.51, -197.25) * mm});
            skLineSegment(sketch, "E25.right", {"start": v(-10.81, -178.35) * mm, "end": v(-10.81, -197.25) * mm});
            skPoint(sketch, "E25.middle", {"position": v(-66.66, -187.8) * mm});
            skLineSegment(sketch, "E26.1.0.0", {"start": v(-8.51, -178.35) * mm, "end": v(17.74, -178.35) * mm});
            skLineSegment(sketch, "E26.1.0.1", {"start": v(-8.51, -197.25) * mm, "end": v(17.74, -197.25) * mm});
            skLineSegment(sketch, "E26.1.0.2", {"start": v(41.54, -178.35) * mm, "end": v(41.54, -197.25) * mm});
            skPoint(sketch, "E26.1.0.3", {"position": v(4.61, -187.8) * mm});
            skLineSegment(sketch, "E26.1.0.4", {"start": v(20.04, -178.35) * mm, "end": v(41.54, -178.35) * mm});
            skLineSegment(sketch, "E26.1.0.5", {"start": v(20.04, -197.25) * mm, "end": v(41.54, -197.25) * mm});
            skLineSegment(sketch, "E26.1.0.6", {"start": v(17.74, -178.35) * mm, "end": v(17.74, -197.25) * mm});
            skLineSegment(sketch, "E26.1.0.7", {"start": v(20.04, -178.35) * mm, "end": v(20.04, -197.25) * mm});
            skLineSegment(sketch, "E26.1.0.8", {"start": v(43.84, -178.35) * mm, "end": v(70.09, -178.35) * mm});
            skLineSegment(sketch, "E26.1.0.9", {"start": v(70.09, -178.35) * mm, "end": v(70.09, -197.25) * mm});
            skPoint(sketch, "E26.1.0.10", {"position": v(30.79, -187.8) * mm});
            skPoint(sketch, "E26.1.0.11", {"position": v(56.96, -187.8) * mm});
            skLineSegment(sketch, "E26.1.0.12", {"start": v(43.84, -197.25) * mm, "end": v(70.09, -197.25) * mm});
            skLineSegment(sketch, "E26.1.0.13", {"start": v(43.84, -178.35) * mm, "end": v(43.84, -197.25) * mm});
            skLineSegment(sketch, "E26.1.0.14", {"start": v(-8.51, -178.35) * mm, "end": v(-8.51, -197.25) * mm});
            skLineSegment(sketch, "E27.bottom", {"start": v(-214.41, -80.25) * mm, "end": v(75.05, -80.25) * mm});
            skLineSegment(sketch, "E27.top", {"start": v(-214.41, -208.25) * mm, "end": v(75.05, -208.25) * mm});
            skLineSegment(sketch, "E27.left", {"start": v(-214.41, -80.25) * mm, "end": v(-214.41, -208.25) * mm});
            skLineSegment(sketch, "E28", {"start": v(75.05, -80.25) * mm, "end": v(75.05, -87.25) * mm});
            skLineSegment(sketch, "E29", {"start": v(75.05, -201.25) * mm, "end": v(75.05, -208.25) * mm});
            skLineSegment(sketch, "E30", {"start": v(75.05, -87.25) * mm, "end": v(75.05, -201.25) * mm});
            skSolve(sketch);
        }
        {
            var Q0;
            Q0=makeQuery(id+"F0.imprint","IMPRINT",FACE,{"disambiguationData":[TD([[makeQuery(id+"F0.imprint","IMPRINT",EDGE,{"derivedFrom":sQuery(id+"F0.wireOp",EDGE,"E0.bottom")}),-1.0]])]});
            var Q1;
            Q1=makeQuery(id+"F0.imprint","IMPRINT",FACE,{"disambiguationData":[TD([[makeQuery(id+"F0.imprint","IMPRINT",EDGE,{"derivedFrom":sQuery(id+"F0.wireOp",EDGE,"E1.bottom")}),1.0]])]});
            extrude(context, id + "F1", {"entities" : qUnion([Q0, Q1]), "depth" : 3 * mm, "offsetDistance" : 25 * mm});
        }
    });
